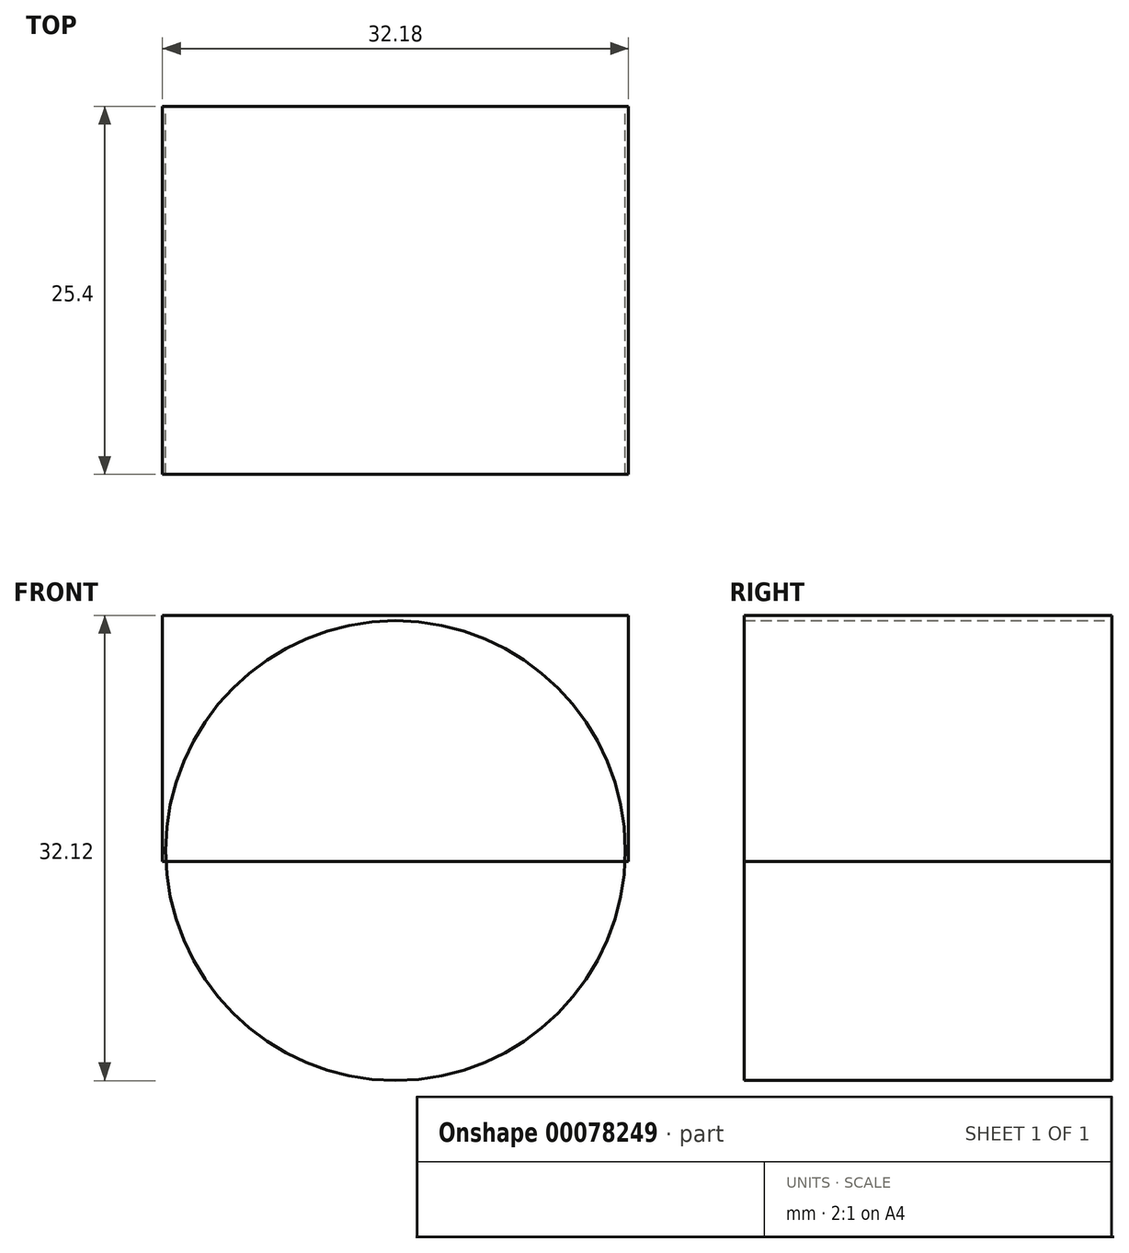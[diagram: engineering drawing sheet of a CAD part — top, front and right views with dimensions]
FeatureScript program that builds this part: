
annotation { "Feature Type Name" : "Feature", "Feature Type Description" : "" }
export const myFeature = defineFeature(function(context is Context, id is Id, definition is map)
    precondition{}
    {
        {
            var Q0;
            Q0=qCreatedBy(makeId("Front.planeOp"),FACE);
            var sketch = newSketch(context, id + "F0", { "sketchPlane" : qUnion([Q0])});
            skCircle(sketch, "E0", {"center": v(0, 0) * mm, "radius": 15.88 * mm});
            skSolve(sketch);
        }
        {
            var Q0;
            Q0=qCreatedBy(makeId("Front.planeOp"),FACE);
            var sketch = newSketch(context, id + "F1", { "sketchPlane" : qUnion([Q0])});
            skLineSegment(sketch, "E1.bottom", {"start": v(-16.1, 16.24) * mm, "end": v(16.1, 16.24) * mm});
            skLineSegment(sketch, "E1.top", {"start": v(-16.1, -0.76) * mm, "end": v(16.1, -0.76) * mm});
            skLineSegment(sketch, "E1.left", {"start": v(-16.1, 16.24) * mm, "end": v(-16.1, -0.76) * mm});
            skLineSegment(sketch, "E1.right", {"start": v(16.1, 16.24) * mm, "end": v(16.1, -0.76) * mm});
            skPoint(sketch, "E1.middle", {"position": v(0, 7.74) * mm});
            skSolve(sketch);
        }
        {
            var Q0;
            Q0=makeQuery(id+"F0.imprint","IMPRINT",FACE,{"disambiguationData":[TD([[makeQuery(id+"F0.imprint","IMPRINT",EDGE,{"derivedFrom":sQuery(id+"F0.wireOp",EDGE,"E0")}),1.0]])]});
            var Q1;
            Q1 = qSketchRegion(id + "F1", true);
            extrude(context, id + "F2", {"entities" : qUnion([Q0, Q1]), "depth" : 25.4 * mm});
        }
    });
